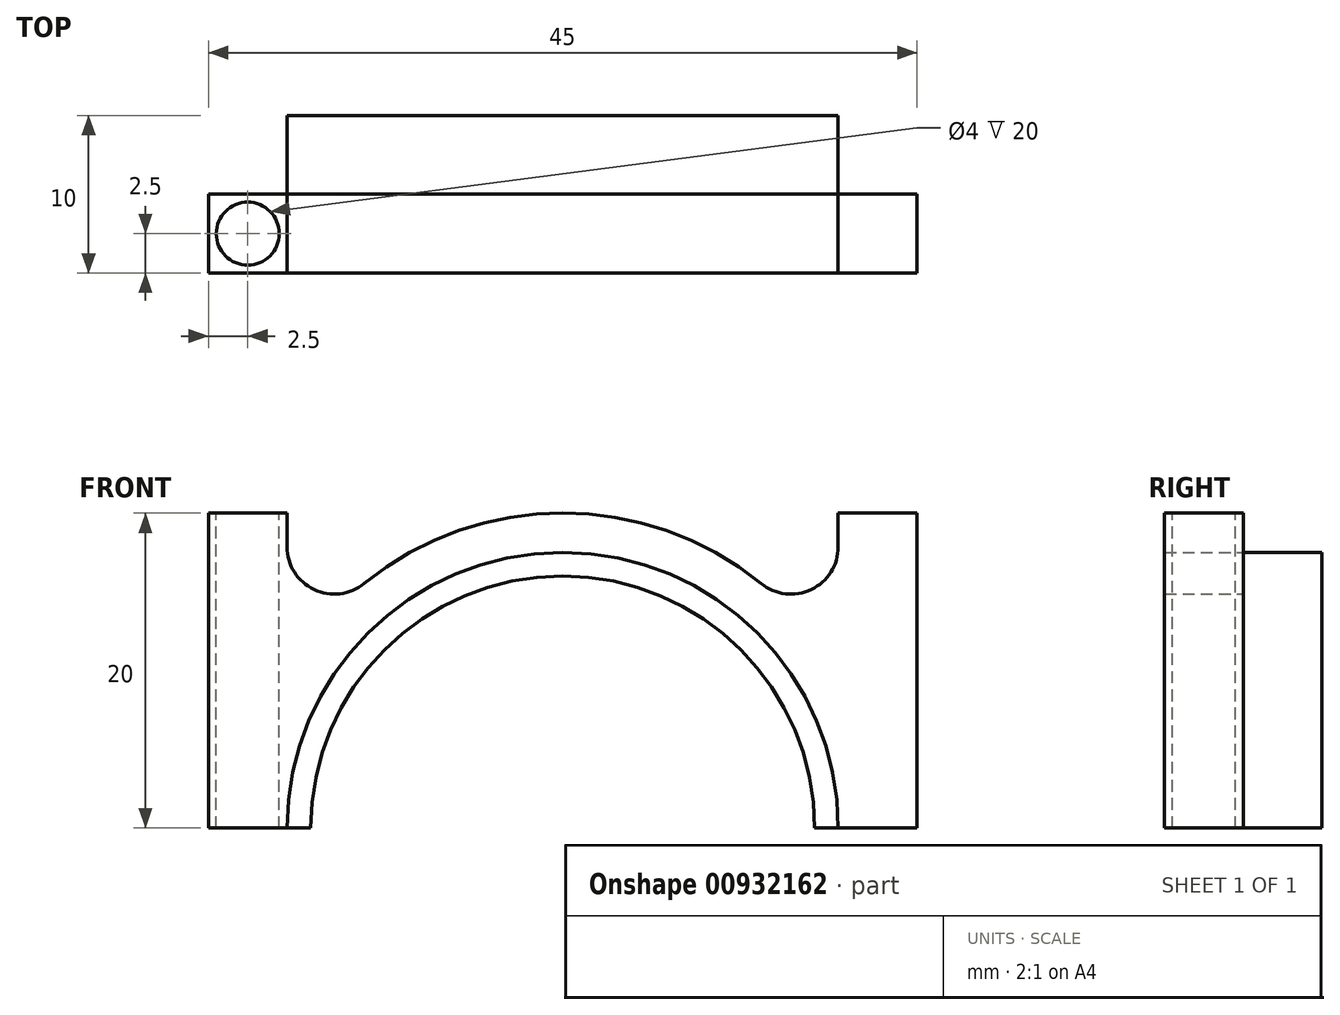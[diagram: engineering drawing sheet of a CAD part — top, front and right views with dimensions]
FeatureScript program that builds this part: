
annotation { "Feature Type Name" : "Feature", "Feature Type Description" : "" }
export const myFeature = defineFeature(function(context is Context, id is Id, definition is map)
    precondition{}
    {
        {
            var Q0;
            Q0=qCreatedBy(makeId("Front.planeOp"),FACE);
            var sketch = newSketch(context, id + "F0", { "sketchPlane" : qUnion([Q0])});
            skArc(sketch, "E0", {"start": v(17.5, 0) * mm, "mid": v(0, 17.5) * mm, "end": v(-17.5, 0) * mm});
            skArc(sketch, "E1", {"start": v(12.6, 15.52) * mm, "mid": v(0, 20) * mm, "end": v(-12.6, 15.52) * mm});
            skLineSegment(sketch, "E2.bottom", {"start": v(-17.5, 0) * mm, "end": v(-22.5, 0) * mm});
            skLineSegment(sketch, "E2.top", {"start": v(-17.5, 20) * mm, "end": v(-22.5, 20) * mm});
            skLineSegment(sketch, "E2.left", {"start": v(-17.5, 17.85) * mm, "end": v(-17.5, 20) * mm});
            skLineSegment(sketch, "E2.right", {"start": v(-22.5, 0) * mm, "end": v(-22.5, 20) * mm});
            skLineSegment(sketch, "E3.MirrorCS", {"start": v(17.5, 20) * mm, "end": v(22.5, 20) * mm});
            skLineSegment(sketch, "E4.MirrorCS", {"start": v(22.5, 0) * mm, "end": v(22.5, 20) * mm});
            skLineSegment(sketch, "E5.MirrorCS", {"start": v(17.5, 0) * mm, "end": v(22.5, 0) * mm});
            skPoint(sketch, "E6.orphan", {"position": v(17.5, 0) * mm});
            skArc(sketch, "E7.MirrorCS", {"start": v(-12.6, 15.52) * mm, "mid": v(0, 20) * mm, "end": v(12.6, 15.52) * mm});
            skLineSegment(sketch, "E8.MirrorCS", {"start": v(17.5, 17.85) * mm, "end": v(17.5, 20) * mm});
            skPoint(sketch, "E9.visualSharp", {"position": v(-17.5, 9.68) * mm});
            skArc(sketch, "E9.filletArc", {"start": v(-17.5, 17.85) * mm, "mid": v(-15.79, 15.14) * mm, "end": v(-12.6, 15.52) * mm});
            skArc(sketch, "E10.MirrorCS", {"start": v(17.5, 17.85) * mm, "mid": v(15.79, 15.14) * mm, "end": v(12.6, 15.52) * mm});
            skPoint(sketch, "E11.orphan", {"position": v(17.5, 9.68) * mm});
            skPoint(sketch, "E12.MirrorCS.end.orphan", {"position": v(17.5, 20) * mm});
            skSolve(sketch);
        }
        {
            var Q0;
            Q0=makeQuery(id+"F0.imprint","IMPRINT",FACE,{"disambiguationData":[TD([[makeQuery(id+"F0.imprint","IMPRINT",EDGE,{"derivedFrom":sQuery(id+"F0.wireOp",EDGE,"E0")}),-1.0]])]});
            extrude(context, id + "F1", {"entities" : qUnion([Q0]), "depth" : 5 * mm, "offsetDistance" : 25.4 * mm});
        }
        {
            var Q0;
            Q0=makeQuery(id+"F1.opExtrude","SWEPT_FACE",FACE,{"disambiguationData":[OSD([sQuery(id+"F0.wireOp",EDGE,"E2.top")])]});
            var sketch = newSketch(context, id + "F2", { "sketchPlane" : qUnion([Q0])});
            skCircle(sketch, "E13", {"center": v(-20, -2.5) * mm, "radius": 2 * mm});
            skPoint(sketch, "E13.centerSnap0", {"position": v(-20, 0) * mm});
            skPoint(sketch, "E13.centerSnap1", {"position": v(-17.5, -2.5) * mm});
            skSolve(sketch);
        }
        {
            var Q0;
            Q0 = qSketchRegion(id + "F2", true);
            extrude(context, id + "F3", {"entities" : qUnion([Q0]), "operationType" : NewBodyOperationType.REMOVE, "endBound" : BoundingType.THROUGH_ALL, "oppositeDirection" : true, "depth" : 25.4 * mm, "offsetDistance" : 25.4 * mm});
        }
        {
            var Q0;
            Q0=qCreatedBy(makeId("Front.planeOp"),FACE);
            var sketch = newSketch(context, id + "F4", { "sketchPlane" : qUnion([Q0])});
            skArc(sketch, "E14", {"start": v(16, 0) * mm, "mid": v(0, 16) * mm, "end": v(-16, 0) * mm});
            skArc(sketch, "E15", {"start": v(17.5, 0) * mm, "mid": v(0, 17.5) * mm, "end": v(-17.5, 0) * mm});
            skLineSegment(sketch, "E16", {"start": v(-17.5, 0) * mm, "end": v(-16, 0) * mm});
            skLineSegment(sketch, "E17.trimOffspring", {"start": v(16, 0) * mm, "end": v(17.5, 0) * mm});
            skSolve(sketch);
        }
        {
            var Q0;
            Q0=makeQuery(id+"F4.imprint","IMPRINT",FACE,{"disambiguationData":[TD([[makeQuery(id+"F4.imprint","IMPRINT",EDGE,{"derivedFrom":sQuery(id+"F4.wireOp",EDGE,"E14")}),-1.0]])]});
            extrude(context, id + "F5", {"entities" : qUnion([Q0]), "endBound" : BoundingType.SYMMETRIC, "depth" : 10 * mm, "offsetDistance" : 25.4 * mm});
        }
    });
